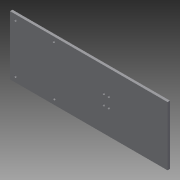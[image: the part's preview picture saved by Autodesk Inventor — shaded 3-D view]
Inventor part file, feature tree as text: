
AUTODESK INVENTOR PART (.ipt)
format: ipt  version: 2014 SP1 (Build 180222100, 222)  size: 103,424 bytes
history: native  units: in
note: dims shown in document units (in); Inventor stores cm internally (conversion verified against a paired STEP export)
features: sketch x2, extrude x1, hole x1
ambient origin geometry x8: Origin, YZ Plane, XZ Plane, XY Plane, X Axis, Y Axis, Z Axis, Center Point
bodies: Body1 (feature_tree)
feature tree (4):
  extrude  "Extrusion2"  Depth=6.0in
  hole  "Hole1"  [1 undecoded]
  sketch  "Sketch1"  dims[d0=16.0in d1=6.0in]
  sketch  "Sketch2"  dims[d2=0.75in d3=45.0deg d4=0.75in d5=45.0deg d6=5.0in d7=0.75in d8=0.25in d10=0.25in d11=0.25in d15=5.0in d16=0.25in d17=0.25in d18=0.0in d19=6.5in d20=0.5in d21=0.5in d22=0.5in d23=0.5in d24=1.0in d25=0.25in d26=0.75in d27=0.375in d28=0.25in d29=0.5635in d30=1.0in d31=0.8108in]
note: 1 required parameter value undecoded (feature->parameter linkage not recoverable at this tier; creation-order binding heuristic only, values carry confidence <= 0.55)
